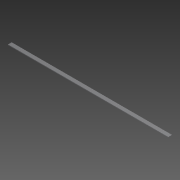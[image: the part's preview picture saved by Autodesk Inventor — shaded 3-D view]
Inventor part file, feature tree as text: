
AUTODESK INVENTOR PART (.ipt)
format: ipt  version: 2013 (Build 170138000, 138)  size: 64,000 bytes
history: native  units: in
note: dims shown in document units (in); Inventor stores cm internally (conversion verified against a paired STEP export)
features: extrude x1, sketch x1
ambient origin geometry x8: Origin, YZ Plane, XZ Plane, XY Plane, X Axis, Y Axis, Z Axis, Center Point
bodies: Solid1 (feature_tree)
feature tree (2):
  extrude  "Extrusion1"  Depth=1.213in
  sketch  "Sketch1"  dims[d0=53.0in d1=1.213in d2=0.2125in d3=0.0in]
